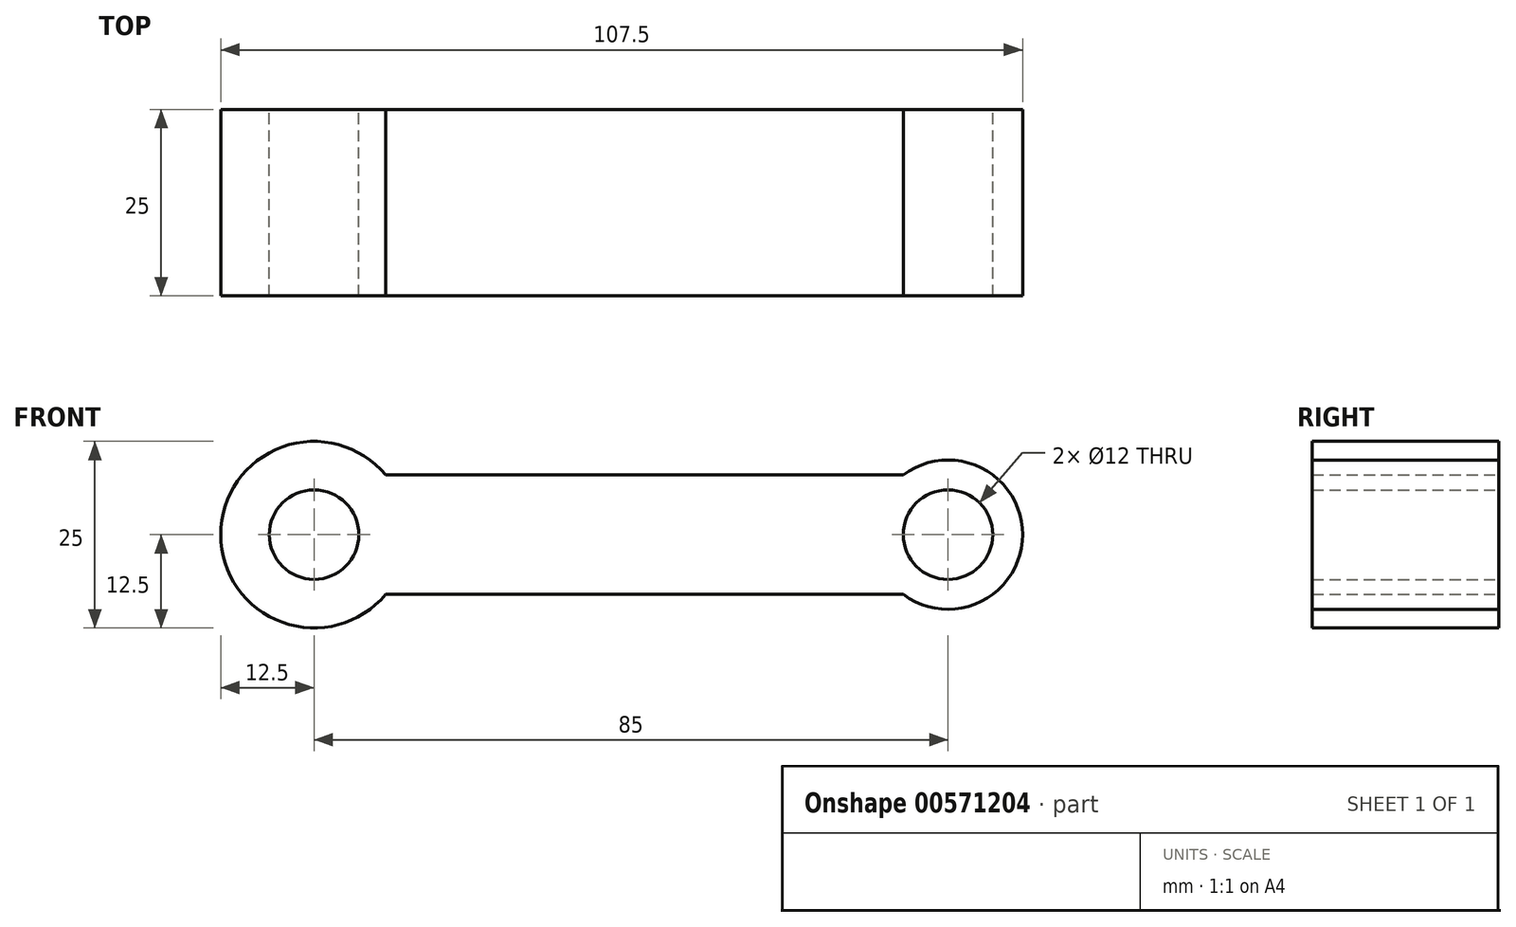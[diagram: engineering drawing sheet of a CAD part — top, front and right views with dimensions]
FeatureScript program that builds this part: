
annotation { "Feature Type Name" : "Feature", "Feature Type Description" : "" }
export const myFeature = defineFeature(function(context is Context, id is Id, definition is map)
    precondition{}
    {
        {
            var Q0;
            Q0=qCreatedBy(makeId("Front.planeOp"),FACE);
            var sketch = newSketch(context, id + "F0", { "sketchPlane" : qUnion([Q0])});
            skCircle(sketch, "E0", {"center": v(0, 0) * mm, "radius": 12.5 * mm});
            skCircle(sketch, "E1", {"center": v(85, 0) * mm, "radius": 10 * mm});
            skLineSegment(sketch, "E2", {"start": v(0, 0) * mm, "end": v(85, 0) * mm, "construction": true});
            skLineSegment(sketch, "E3", {"start": v(9.6, 8) * mm, "end": v(79, 8) * mm});
            skLineSegment(sketch, "E4.MirrorCS", {"start": v(9.6, -8) * mm, "end": v(79, -8) * mm});
            skCircle(sketch, "E5", {"center": v(0, 0) * mm, "radius": 6 * mm});
            skCircle(sketch, "E6", {"center": v(85, 0) * mm, "radius": 6 * mm});
            skSolve(sketch);
        }
        {
            var Q0;
            Q0 = qSketchRegion(id + "F0", true);
            extrude(context, id + "F1", {"entities" : qUnion([Q0]), "depth" : 25 * mm, "offsetDistance" : 25 * mm});
        }
    });
